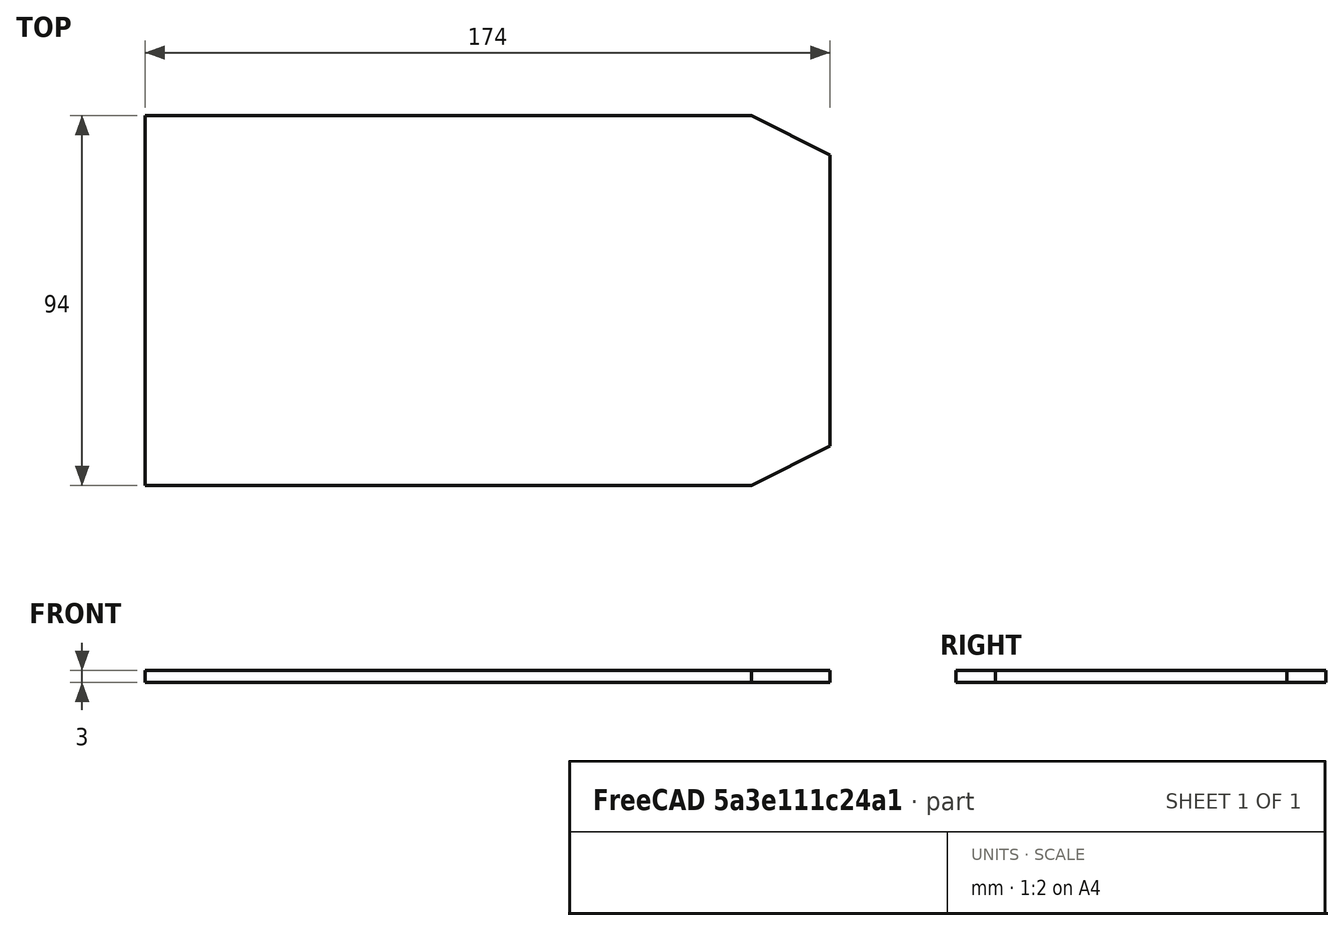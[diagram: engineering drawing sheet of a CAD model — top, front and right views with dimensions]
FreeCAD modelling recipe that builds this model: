
FCSTD DOCUMENT  (FreeCAD 0.16R6706 (Git))
Label: master-base(2)
License: All rights reserved
LicenseURL: http://en.wikipedia.org/wiki/All_rights_reserved
objects: Sketcher::SketchObject×1, PartDesign::Pad×1
note: 3 computed .brp shape members not serialized (recipe doc carries the construction recipe); baked Part::Feature solids carry a one-line shape summary decoded from their .brp

FEATURE [Sketcher::SketchObject] Sketch
  sketch-geometry (6):
    g0: LineSegment StartX=-26 StartY=47 StartZ=0 EndX=-26 EndY=-47 EndZ=0
    g1: LineSegment StartX=-26 StartY=-47 StartZ=0 EndX=128 EndY=-47 EndZ=0
    g2: LineSegment StartX=128 StartY=47 StartZ=0 EndX=-26 EndY=47 EndZ=0
    g3: LineSegment StartX=148 StartY=37 StartZ=0 EndX=148 EndY=-37 EndZ=0
    g4: LineSegment StartX=128 StartY=47 StartZ=0 EndX=148 EndY=37 EndZ=0
    g5: LineSegment StartX=148 StartY=-37 StartZ=0 EndX=128 EndY=-47 EndZ=0
  constraints (16):
    c: Coincident(g0,g1)
    c: Coincident(g2,g0)
    c: Vertical(g0)
    c: Horizontal(g1)
    c: Horizontal(g2)
    c: DistanceX(g0,g-1) = 26
    c: DistanceX(g-1,g2) = 128
    c: Symmetric(g1,g2,g-1)
    c: DistanceY(g-1,g0) = 47
    c: DistanceX(g2,g3) = 20
    c: Symmetric(g3,g3,g-1)
    c: DistanceY(g3,g2) = 10
    c: Coincident(g2,g4)
    c: Coincident(g3,g4)
    c: Coincident(g3,g5)
    c: Coincident(g1,g5)
FEATURE [PartDesign::Pad] Pad
  Length = 3
  Length2 = 100
  Sketch = -> Sketch
  Type = 0
